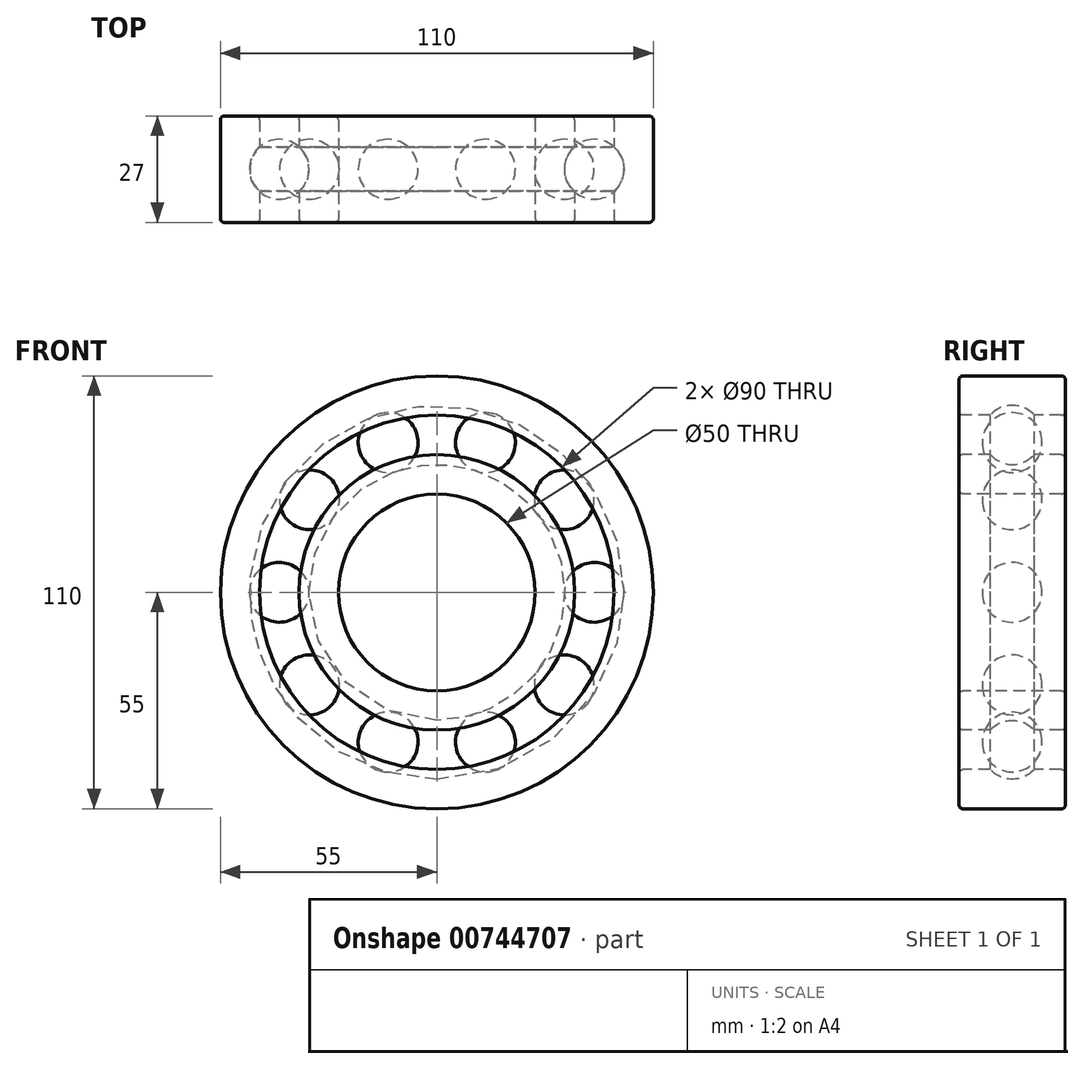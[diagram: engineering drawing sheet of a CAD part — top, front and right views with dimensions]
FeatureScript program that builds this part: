
annotation { "Feature Type Name" : "Feature", "Feature Type Description" : "" }
export const myFeature = defineFeature(function(context is Context, id is Id, definition is map)
    precondition{}
    {
        {
            var Q0;
            Q0=qCreatedBy(makeId("Top.planeOp"),FACE);
            var sketch = newSketch(context, id + "F0", { "sketchPlane" : qUnion([Q0])});
            skLineSegment(sketch, "E0.bottom", {"start": v(26, 13.5) * mm, "end": v(34, 13.5) * mm});
            skLineSegment(sketch, "E0.top", {"start": v(26, -13.5) * mm, "end": v(34, -13.5) * mm});
            skLineSegment(sketch, "E0.left", {"start": v(25, 12.5) * mm, "end": v(25, -12.5) * mm});
            skLineSegment(sketch, "E0.right", {"start": v(35, 12.5) * mm, "end": v(35, 5.6) * mm});
            skLineSegment(sketch, "E1.bottom", {"start": v(46, 13.5) * mm, "end": v(54, 13.5) * mm});
            skLineSegment(sketch, "E1.top", {"start": v(46, -13.5) * mm, "end": v(54, -13.5) * mm});
            skLineSegment(sketch, "E1.left", {"start": v(45, 12.5) * mm, "end": v(45, 5.6) * mm});
            skLineSegment(sketch, "E1.right", {"start": v(55, 12.5) * mm, "end": v(55, -12.5) * mm});
            skCircle(sketch, "E2", {"center": v(40, 0) * mm, "radius": 7.5 * mm});
            skLineSegment(sketch, "E3.trimOffspring", {"start": v(35, -5.6) * mm, "end": v(35, -12.5) * mm});
            skLineSegment(sketch, "E4.trimOffspring", {"start": v(45, -5.6) * mm, "end": v(45, -12.5) * mm});
            skLineSegment(sketch, "E5", {"start": v(40, 11.67) * mm, "end": v(40, -13.5) * mm});
            skLineSegment(sketch, "E6", {"start": v(0, -36.1) * mm, "end": v(0, 26.97) * mm});
            skPoint(sketch, "E7.visualSharp", {"position": v(55, -13.5) * mm});
            skArc(sketch, "E7.filletArc", {"start": v(54, -13.5) * mm, "mid": v(54.7, -13.2) * mm, "end": v(55, -12.5) * mm});
            skPoint(sketch, "E8.visualSharp", {"position": v(55, 13.5) * mm});
            skArc(sketch, "E8.filletArc", {"start": v(55, 12.5) * mm, "mid": v(54.7, 13.2) * mm, "end": v(54, 13.5) * mm});
            skPoint(sketch, "E9.visualSharp", {"position": v(45, 13.5) * mm});
            skArc(sketch, "E9.filletArc", {"start": v(46, 13.5) * mm, "mid": v(45.3, 13.2) * mm, "end": v(45, 12.5) * mm});
            skPoint(sketch, "E10.visualSharp", {"position": v(45, -13.5) * mm});
            skArc(sketch, "E10.filletArc", {"start": v(45, -12.5) * mm, "mid": v(45.3, -13.2) * mm, "end": v(46, -13.5) * mm});
            skPoint(sketch, "E11.visualSharp", {"position": v(35, -13.5) * mm});
            skArc(sketch, "E11.filletArc", {"start": v(34, -13.5) * mm, "mid": v(34.7, -13.2) * mm, "end": v(35, -12.5) * mm});
            skPoint(sketch, "E12.visualSharp", {"position": v(35, 13.5) * mm});
            skArc(sketch, "E12.filletArc", {"start": v(35, 12.5) * mm, "mid": v(34.7, 13.2) * mm, "end": v(34, 13.5) * mm});
            skPoint(sketch, "E13.visualSharp", {"position": v(25, 13.5) * mm});
            skArc(sketch, "E13.filletArc", {"start": v(26, 13.5) * mm, "mid": v(25.3, 13.2) * mm, "end": v(25, 12.5) * mm});
            skPoint(sketch, "E14.visualSharp", {"position": v(25, -13.5) * mm});
            skArc(sketch, "E14.filletArc", {"start": v(25, -12.5) * mm, "mid": v(25.3, -13.2) * mm, "end": v(26, -13.5) * mm});
            skSolve(sketch);
        }
        {
            var Q0;
            Q0=makeQuery(id+"F0.imprint","IMPRINT",FACE,{"disambiguationData":[TD([[makeQuery(id+"F0.imprint","IMPRINT",EDGE,{"derivedFrom":sQuery(id+"F0.wireOp",EDGE,"E0.bottom")}),-1.0]])]});
            var Q1;
            Q1=makeQuery(id+"F0.imprint","IMPRINT",FACE,{"disambiguationData":[TD([[makeQuery(id+"F0.imprint","IMPRINT",EDGE,{"derivedFrom":sQuery(id+"F0.wireOp",EDGE,"E1.bottom")}),-1.0]])]});
            var Q2;
            Q2=sQuery(id+"F0.wireOp",EDGE,"E6");
            revolve(context, id + "F1", {"surfaceOperationType" : NewSurfaceOperationType.NEW, "entities" : qUnion([Q0, Q1]), "axis" : qUnion([Q2]), "revolveType" : RevolveType.FULL});
        }
        {
            var Q0;
            Q0=qCreatedBy(makeId("Top.planeOp"),FACE);
            var sketch = newSketch(context, id + "F2", { "sketchPlane" : qUnion([Q0])});
            skCircle(sketch, "E15.0", {"center": v(40, 0) * mm, "radius": 7.6 * mm});
            skLineSegment(sketch, "E16", {"start": v(40, 15.66) * mm, "end": v(40, -18.62) * mm});
            skSolve(sketch);
        }
        {
            var Q0;
            {var subQ0=sQuery(id+"F2.wireOp",EDGE,"E16");var subQ1=sQuery(id+"F2.wireOp",EDGE,"E15.0");var subQ2=makeQuery(id+"F2.imprint","INTERSECT",VERTEX,{"disambiguationData":[OD(0.0)],"derivedFrom":[subQ1,subQ0]});Q0=makeQuery(id+"F2.imprint","IMPRINT",FACE,{"disambiguationData":[TD([[makeQuery(id+"F2.imprint","IMPRINT",EDGE,{"disambiguationData":[TD([[subQ2,1.0]])],"derivedFrom":subQ1}),1.0]])]});}
            var Q1;
            Q1=sQuery(id+"F2.wireOp",EDGE,"E16");
            revolve(context, id + "F3", {"surfaceOperationType" : NewSurfaceOperationType.NEW, "entities" : qUnion([Q0]), "axis" : qUnion([Q1]), "revolveType" : RevolveType.FULL});
        }
        {
            var Q0;
            Q0=makeQuery(id+"F3.opRevolve","SWEPT_BODY",BODY,{"disambiguationData":[OSD([sQuery(id+"F2.wireOp",EDGE,"E15.0"),sQuery(id+"F2.wireOp",EDGE,"E16")])]});
            var Q1;
            Q1=sQuery(id+"F0.wireOp",EDGE,"E6");
            circularPattern(context, id + "F4", {"entities" : qUnion([Q0]), "axis" : qUnion([Q1]), "angle" : 360 * degree, "instanceCount" : 10, "equalSpace" : true});
        }
    });
